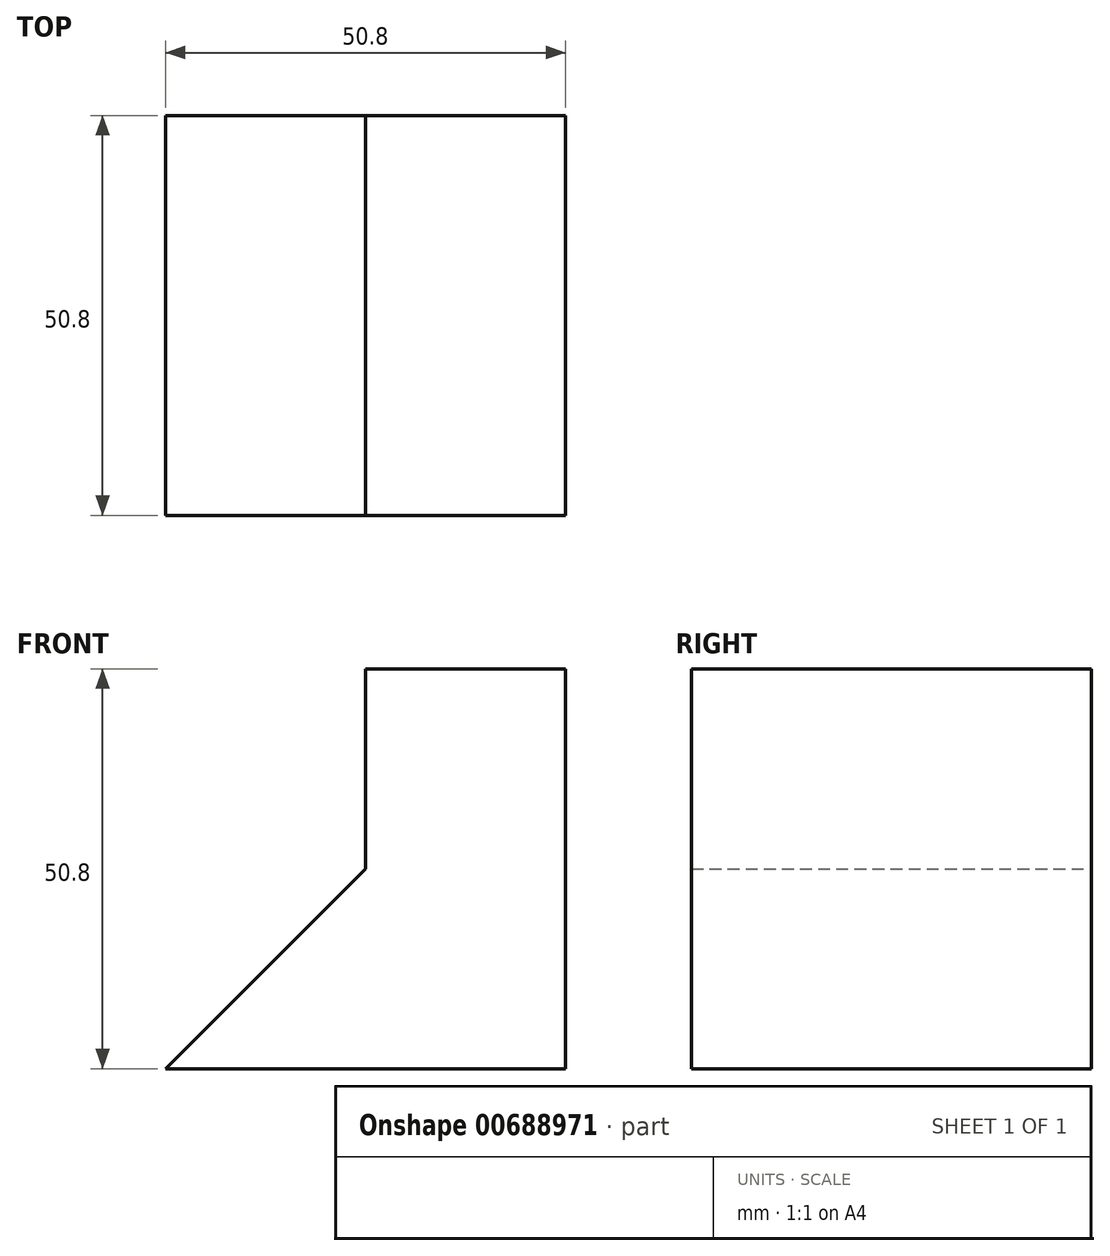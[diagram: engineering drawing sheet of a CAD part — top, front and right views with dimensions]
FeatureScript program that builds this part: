
annotation { "Feature Type Name" : "Feature", "Feature Type Description" : "" }
export const myFeature = defineFeature(function(context is Context, id is Id, definition is map)
    precondition{}
    {
        {
            var Q0;
            Q0=qCreatedBy(makeId("Front.planeOp"),FACE);
            var sketch = newSketch(context, id + "F0", { "sketchPlane" : qUnion([Q0])});
            skLineSegment(sketch, "E0", {"start": v(-66.17, 47.64) * mm, "end": v(-40.77, 47.64) * mm});
            skLineSegment(sketch, "E1", {"start": v(-40.77, 47.64) * mm, "end": v(-40.77, -3.16) * mm});
            skLineSegment(sketch, "E2", {"start": v(-40.77, -3.16) * mm, "end": v(-91.57, -3.16) * mm});
            skLineSegment(sketch, "E3", {"start": v(-66.17, 47.64) * mm, "end": v(-66.17, 22.24) * mm});
            skLineSegment(sketch, "E4", {"start": v(-66.17, 22.24) * mm, "end": v(-91.57, -3.16) * mm});
            skSolve(sketch);
        }
        {
            var Q0;
            Q0=makeQuery(id+"F0.imprint","IMPRINT",FACE,{"disambiguationData":[TD([[makeQuery(id+"F0.imprint","IMPRINT",EDGE,{"derivedFrom":sQuery(id+"F0.wireOp",EDGE,"E0")}),-1.0]])]});
            extrude(context, id + "F1", {"entities" : qUnion([Q0]), "depth" : 50.8 * mm, "offsetDistance" : 25.4 * mm});
        }
    });
